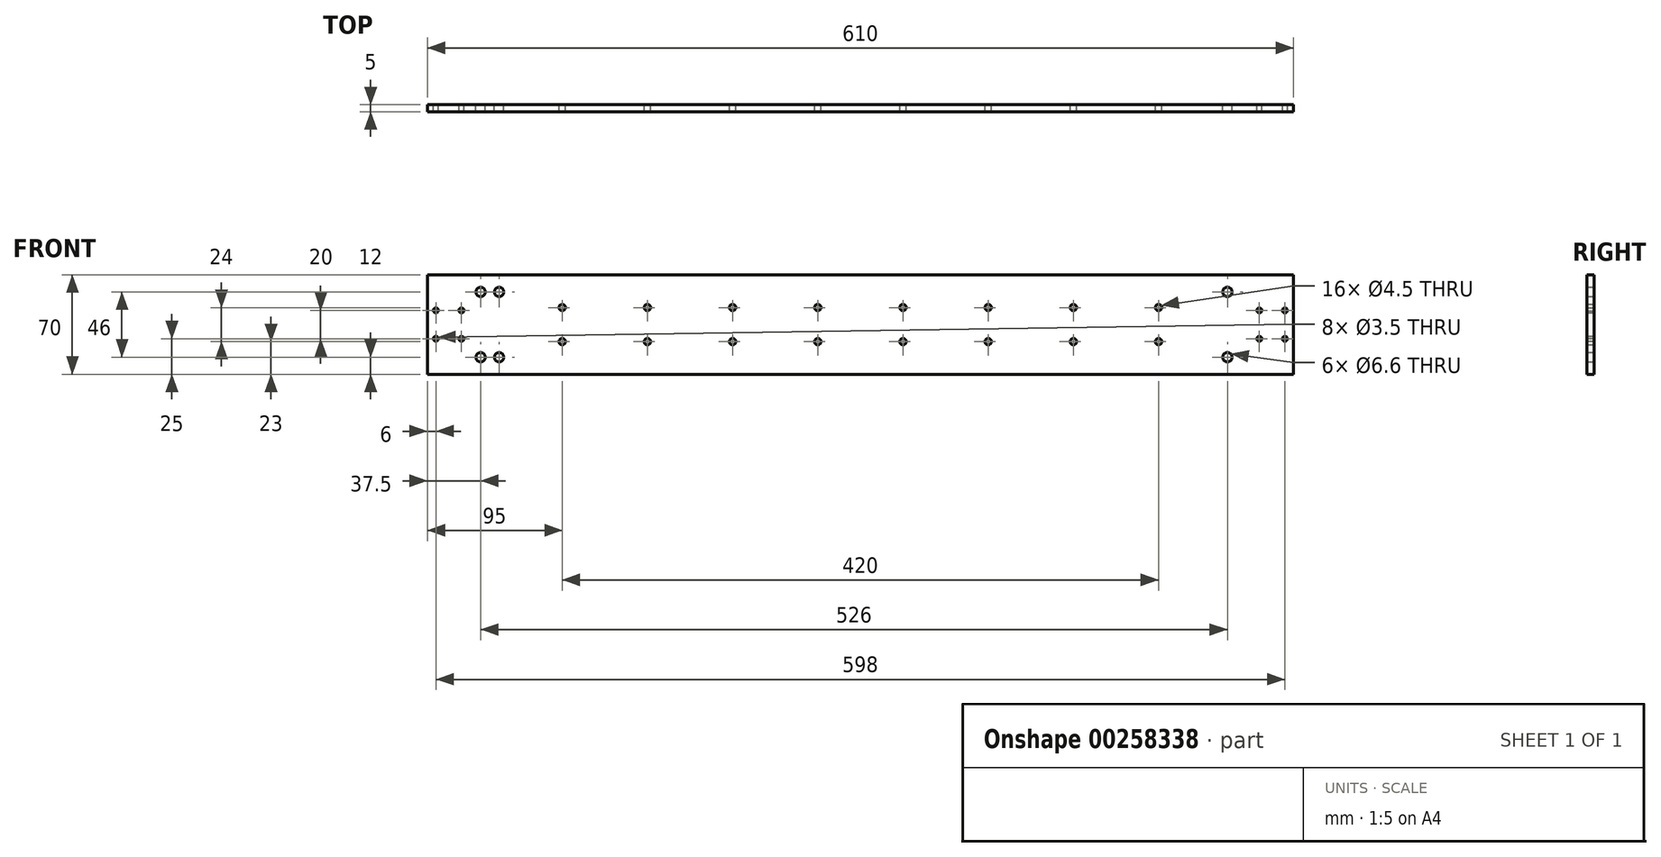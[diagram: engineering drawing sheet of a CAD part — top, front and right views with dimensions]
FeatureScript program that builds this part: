
annotation { "Feature Type Name" : "Feature", "Feature Type Description" : "" }
export const myFeature = defineFeature(function(context is Context, id is Id, definition is map)
    precondition{}
    {
        {
            var Q0;
            Q0=qCreatedBy(makeId("Front.planeOp"),FACE);
            var sketch = newSketch(context, id + "F0", { "sketchPlane" : qUnion([Q0])});
            skLineSegment(sketch, "E0.bottom", {"start": v(15, -21) * mm, "end": v(-15, -21) * mm, "construction": true});
            skLineSegment(sketch, "E0.top", {"start": v(15, 21) * mm, "end": v(-15, 21) * mm, "construction": true});
            skLineSegment(sketch, "E0.left", {"start": v(15, -21) * mm, "end": v(15, 21) * mm, "construction": true});
            skLineSegment(sketch, "E0.right", {"start": v(-15, -21) * mm, "end": v(-15, 21) * mm, "construction": true});
            skPoint(sketch, "E0.middle", {"position": v(0, 0) * mm});
            skLineSegment(sketch, "E1", {"start": v(0, 21) * mm, "end": v(0, -21) * mm, "construction": true});
            skLineSegment(sketch, "E2", {"start": v(-15, 0) * mm, "end": v(15, 0) * mm, "construction": true});
            skCircle(sketch, "E3", {"center": v(9, 10) * mm, "radius": 1.75 * mm});
            skCircle(sketch, "E4.MirrorC", {"center": v(-9, 10) * mm, "radius": 1.75 * mm});
            skCircle(sketch, "E5.MirrorC", {"center": v(-9, -10) * mm, "radius": 1.75 * mm});
            skCircle(sketch, "E6.MirrorC", {"center": v(9, -10) * mm, "radius": 1.75 * mm});
            skLineSegment(sketch, "E7", {"start": v(-15, 21) * mm, "end": v(-290, 21) * mm, "construction": true});
            skLineSegment(sketch, "E8", {"start": v(-290, 21) * mm, "end": v(-290, -21) * mm, "construction": true});
            skLineSegment(sketch, "E9", {"start": v(-290, -21) * mm, "end": v(-15, -21) * mm});
            skLineSegment(sketch, "E10.MirrorCS", {"start": v(-595, -21) * mm, "end": v(-565, -21) * mm, "construction": true});
            skLineSegment(sketch, "E11.MirrorCS", {"start": v(-595, 21) * mm, "end": v(-565, 21) * mm, "construction": true});
            skLineSegment(sketch, "E12.MirrorCS", {"start": v(-565, 21) * mm, "end": v(-290, 21) * mm, "construction": true});
            skLineSegment(sketch, "E13.MirrorCS", {"start": v(-290, -21) * mm, "end": v(-565, -21) * mm, "construction": true});
            skCircle(sketch, "E14.MirrorC", {"center": v(-589, -10) * mm, "radius": 1.75 * mm});
            skPoint(sketch, "E15.MirrorP", {"position": v(-580, 0) * mm});
            skLineSegment(sketch, "E16.MirrorCS", {"start": v(-565, -21) * mm, "end": v(-565, 21) * mm, "construction": true});
            skLineSegment(sketch, "E17.MirrorCS", {"start": v(-580, 21) * mm, "end": v(-580, -21) * mm, "construction": true});
            skCircle(sketch, "E18.MirrorC", {"center": v(-571, -10) * mm, "radius": 1.75 * mm});
            skCircle(sketch, "E19.MirrorC", {"center": v(-571, 10) * mm, "radius": 1.75 * mm});
            skCircle(sketch, "E20.MirrorC", {"center": v(-589, 10) * mm, "radius": 1.75 * mm});
            skLineSegment(sketch, "E21.MirrorCS", {"start": v(-595, -21) * mm, "end": v(-595, 21) * mm, "construction": true});
            skLineSegment(sketch, "E22.MirrorCS", {"start": v(-565, 0) * mm, "end": v(-595, 0) * mm, "construction": true});
            skLineSegment(sketch, "E23", {"start": v(-565, 0) * mm, "end": v(-15, 0) * mm, "construction": true});
            skCircle(sketch, "E24", {"center": v(-320, 12) * mm, "radius": 2.25 * mm});
            skCircle(sketch, "E25", {"center": v(-380, 12) * mm, "radius": 2.25 * mm});
            skCircle(sketch, "E26", {"center": v(-440, 12) * mm, "radius": 2.25 * mm});
            skCircle(sketch, "E27", {"center": v(-500, 12) * mm, "radius": 2.25 * mm});
            skCircle(sketch, "E28.MirrorC", {"center": v(-500, -12) * mm, "radius": 2.25 * mm});
            skCircle(sketch, "E29.MirrorC", {"center": v(-440, -12) * mm, "radius": 2.25 * mm});
            skCircle(sketch, "E30.MirrorC", {"center": v(-320, -12) * mm, "radius": 2.25 * mm});
            skCircle(sketch, "E31.MirrorC", {"center": v(-380, -12) * mm, "radius": 2.25 * mm});
            skCircle(sketch, "E32.MirrorC", {"center": v(-140, -12) * mm, "radius": 2.25 * mm});
            skCircle(sketch, "E33.MirrorC", {"center": v(-260, 12) * mm, "radius": 2.25 * mm});
            skCircle(sketch, "E34.MirrorC", {"center": v(-200, -12) * mm, "radius": 2.25 * mm});
            skCircle(sketch, "E35.MirrorC", {"center": v(-80, -12) * mm, "radius": 2.25 * mm});
            skCircle(sketch, "E36.MirrorC", {"center": v(-140, 12) * mm, "radius": 2.25 * mm});
            skCircle(sketch, "E37.MirrorC", {"center": v(-80, 12) * mm, "radius": 2.25 * mm});
            skCircle(sketch, "E38.MirrorC", {"center": v(-260, -12) * mm, "radius": 2.25 * mm});
            skCircle(sketch, "E39.MirrorC", {"center": v(-200, 12) * mm, "radius": 2.25 * mm});
            skLineSegment(sketch, "E40.MirrorCS", {"start": v(-15, 0) * mm, "end": v(-565, 0) * mm, "construction": true});
            skLineSegment(sketch, "E41.MirrorCS", {"start": v(-290, -21) * mm, "end": v(-15, -21) * mm, "construction": true});
            skCircle(sketch, "E42", {"center": v(-544.5, 23) * mm, "radius": 3.3 * mm});
            skCircle(sketch, "E43", {"center": v(-31.5, 23) * mm, "radius": 3.3 * mm});
            skCircle(sketch, "E44", {"center": v(-557.5, 23) * mm, "radius": 3.3 * mm});
            skLineSegment(sketch, "E45", {"start": v(-557.5, 23) * mm, "end": v(-544.5, 23) * mm, "construction": true});
            skPoint(sketch, "E46.middle", {"position": v(-551, 23) * mm});
            skLineSegment(sketch, "E47", {"start": v(-551, 23) * mm, "end": v(-551, -23) * mm, "construction": true});
            skLineSegment(sketch, "E48", {"start": v(-563, 0) * mm, "end": v(-539, 0) * mm, "construction": true});
            skPoint(sketch, "E48.startSnap0", {"position": v(-551, 0) * mm});
            skCircle(sketch, "E49.MirrorC", {"center": v(-544.5, -23) * mm, "radius": 3.3 * mm});
            skCircle(sketch, "E50.MirrorC", {"center": v(-557.5, -23) * mm, "radius": 3.3 * mm});
            skLineSegment(sketch, "E51.bottom", {"start": v(-539, -35) * mm, "end": v(-563, -35) * mm});
            skLineSegment(sketch, "E51.top", {"start": v(-539, 35) * mm, "end": v(-563, 35) * mm});
            skLineSegment(sketch, "E51.left", {"start": v(-539, -35) * mm, "end": v(-539, 35) * mm, "construction": true});
            skLineSegment(sketch, "E51.right", {"start": v(-563, -35) * mm, "end": v(-563, 35) * mm, "construction": true});
            skLineSegment(sketch, "E52", {"start": v(-557.5, -23) * mm, "end": v(-544.5, -23) * mm, "construction": true});
            skCircle(sketch, "E53", {"center": v(-31.5, -23) * mm, "radius": 3.3 * mm});
            skLineSegment(sketch, "E54", {"start": v(-31.5, 23) * mm, "end": v(-31.5, -23) * mm, "construction": true});
            skLineSegment(sketch, "E55.bottom", {"start": v(-22, 35) * mm, "end": v(-41, 35) * mm});
            skLineSegment(sketch, "E55.top", {"start": v(-22, -35) * mm, "end": v(-41, -35) * mm});
            skLineSegment(sketch, "E55.left", {"start": v(-22, 35) * mm, "end": v(-22, -35) * mm, "construction": true});
            skLineSegment(sketch, "E55.right", {"start": v(-41, 35) * mm, "end": v(-41, -35) * mm, "construction": true});
            skPoint(sketch, "E55.middle", {"position": v(-31.5, 0) * mm});
            skLineSegment(sketch, "E56.bottom", {"start": v(-41, -35) * mm, "end": v(-539, -35) * mm});
            skLineSegment(sketch, "E56.top", {"start": v(-41, 35) * mm, "end": v(-539, 35) * mm});
            skLineSegment(sketch, "E56.left", {"start": v(-41, -35) * mm, "end": v(-41, 35) * mm, "construction": true});
            skPoint(sketch, "E56.middle", {"position": v(-290, 0) * mm});
            skLineSegment(sketch, "E57", {"start": v(-22, 35) * mm, "end": v(15, 35) * mm});
            skLineSegment(sketch, "E58", {"start": v(15, 35) * mm, "end": v(15, -35) * mm});
            skLineSegment(sketch, "E59", {"start": v(15, -35) * mm, "end": v(-22, -35) * mm});
            skLineSegment(sketch, "E60", {"start": v(-563, 35) * mm, "end": v(-595, 35) * mm});
            skLineSegment(sketch, "E61", {"start": v(-595, 35) * mm, "end": v(-595, -35) * mm});
            skLineSegment(sketch, "E62", {"start": v(-595, -35) * mm, "end": v(-563, -35) * mm});
            skSolve(sketch);
        }
        {
            var Q0;
            Q0=qSketchRegion(id+"F0",true);
            extrude(context, id + "F1", {"entities" : qUnion([Q0]), "depth" : 5 * mm});
        }
    });
